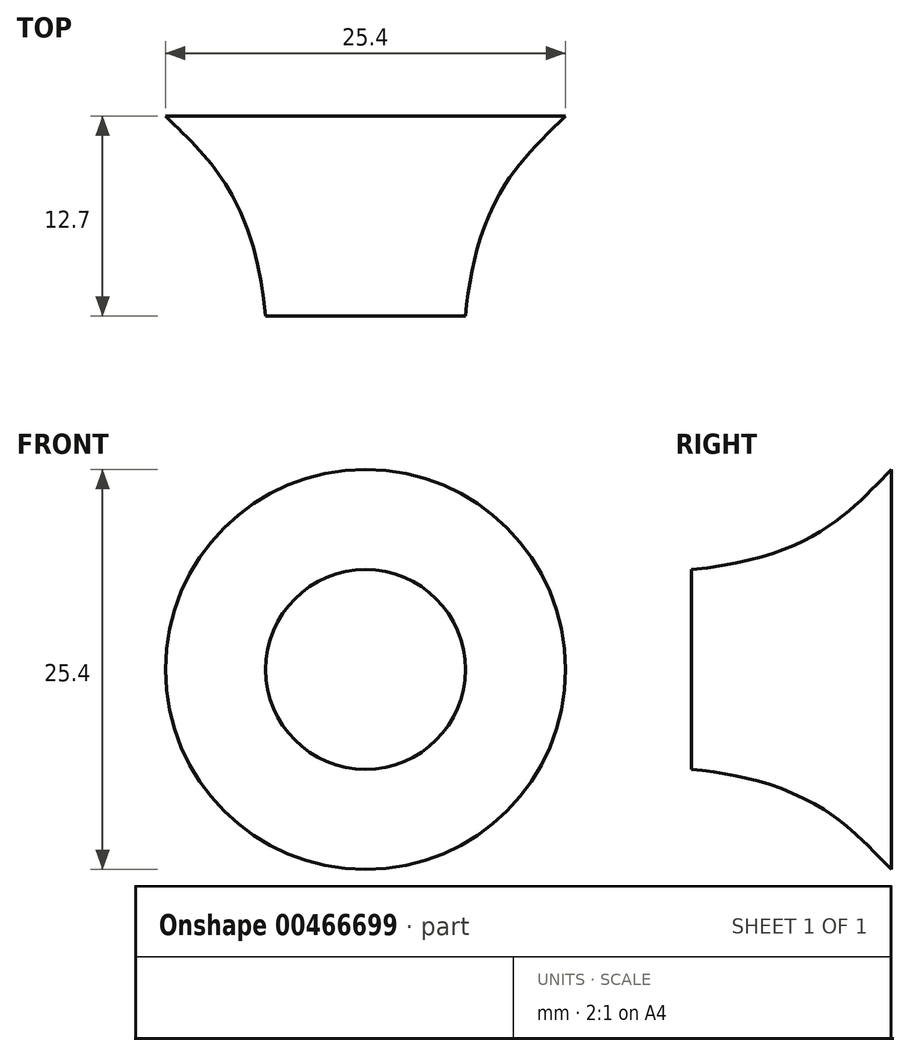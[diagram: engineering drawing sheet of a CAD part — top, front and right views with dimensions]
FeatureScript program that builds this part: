
annotation { "Feature Type Name" : "Feature", "Feature Type Description" : "" }
export const myFeature = defineFeature(function(context is Context, id is Id, definition is map)
    precondition{}
    {
        {
            var Q0;
            Q0=qCreatedBy(makeId("Front.planeOp"),FACE);
            var sketch = newSketch(context, id + "F0", { "sketchPlane" : qUnion([Q0])});
            skCircle(sketch, "E0", {"center": v(0, 0) * mm, "radius": 12.7 * mm});
            skSolve(sketch);
        }
        {
            var Q0;
            Q0=qCreatedBy(makeId("Top.planeOp"),FACE);
            var sketch = newSketch(context, id + "F1", { "sketchPlane" : qUnion([Q0])});
            skLineSegment(sketch, "E1", {"start": v(0, 0) * mm, "end": v(0, -12.7) * mm});
            skLineSegment(sketch, "E2", {"start": v(0, -12.7) * mm, "end": v(6.35, -12.7) * mm});
            skLineSegment(sketch, "E3.0", {"start": v(12.7, 0) * mm, "end": v(-12.7, 0) * mm});
            skFitSpline(sketch, "E4", {"points": [v(12.7, 0) * mm, v(6.35, -12.7) * mm], "startDerivative": vector(-6.94, -7.02) * mm, "endDerivative": vector(-2.14, -23.74) * mm});
            skSolve(sketch);
        }
        {
            var Q0;
            {var subQ0=sQuery(id+"F1.wireOp",EDGE,"E1");Q0=makeQuery(id+"F1.imprint","IMPRINT",FACE,{"disambiguationData":[TD([[makeQuery(id+"F1.imprint","IMPRINT",EDGE,{"derivedFrom":subQ0}),1.0]])]});}
            var Q1;
            Q1=sQuery(id+"F0.wireOp",EDGE,"E0");
            revolve(context, id + "F2", {"entities" : qUnion([Q0]), "axis" : qUnion([Q1]), "revolveType" : RevolveType.FULL});
        }
    });
